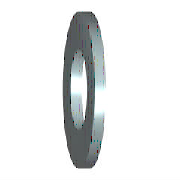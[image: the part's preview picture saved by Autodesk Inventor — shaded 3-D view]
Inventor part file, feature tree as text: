
AUTODESK INVENTOR PART (.ipt)
format: ipt  version: 2022 (Build 260153000, 153)  size: 108,032 bytes
history: native  units: mm (DEFAULTED — no unit token found)
features: other x1, plane x1, sketch x1
ambient origin geometry x7: Origin, YZ Plane, XY Plane, X Axis, Y Axis, Z Axis, Center Point
bodies: Solid1 (feature_tree), Body (feature_tree)
feature tree (3):
  other  "Work Axis1"
  plane  "Work Plane1"
  sketch  "Sketch"  dims[d0=6.4mm d1=12.0mm d2=1.6mm d3=0.0mm d4=0.0mm d5=0.0mm d6=0.0mm d7=0.0mm]
